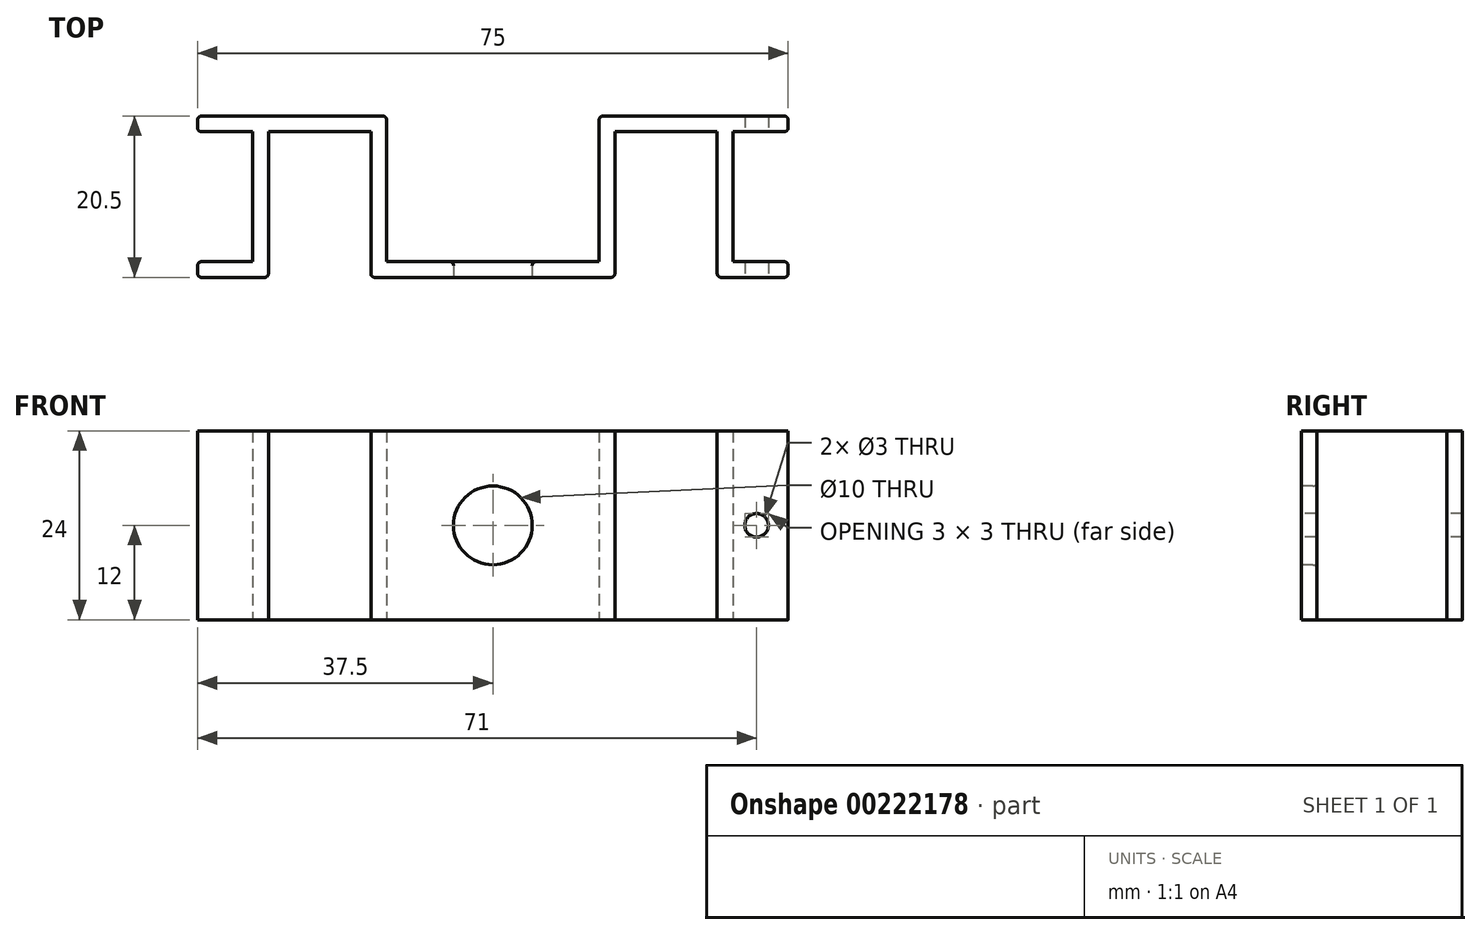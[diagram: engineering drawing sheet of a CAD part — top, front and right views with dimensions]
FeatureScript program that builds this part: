
annotation { "Feature Type Name" : "Feature", "Feature Type Description" : "" }
export const myFeature = defineFeature(function(context is Context, id is Id, definition is map)
    precondition{}
    {
        {
            var Q0;
            Q0=qCreatedBy(makeId("Top.planeOp"),FACE);
            var sketch = newSketch(context, id + "F0", { "sketchPlane" : qUnion([Q0])});
            skLineSegment(sketch, "E0", {"start": v(0, 0) * mm, "end": v(15.5, 0) * mm});
            skLineSegment(sketch, "E1", {"start": v(13.5, 20.5) * mm, "end": v(37.5, 20.5) * mm});
            skLineSegment(sketch, "E2", {"start": v(37.5, 20.5) * mm, "end": v(37.5, 18.5) * mm});
            skLineSegment(sketch, "E3", {"start": v(37.5, 18.5) * mm, "end": v(30.5, 18.5) * mm});
            skLineSegment(sketch, "E4", {"start": v(30.5, 18.5) * mm, "end": v(30.5, 2) * mm});
            skLineSegment(sketch, "E5", {"start": v(30.5, 2) * mm, "end": v(37.5, 2) * mm});
            skLineSegment(sketch, "E6", {"start": v(37.5, 2) * mm, "end": v(37.5, 0) * mm});
            skLineSegment(sketch, "E7", {"start": v(37.5, 0) * mm, "end": v(28.5, 0) * mm});
            skLineSegment(sketch, "E8", {"start": v(28.5, 0) * mm, "end": v(28.5, 18.5) * mm});
            skLineSegment(sketch, "E9", {"start": v(28.5, 18.5) * mm, "end": v(15.5, 18.5) * mm});
            skLineSegment(sketch, "E10", {"start": v(15.5, 18.5) * mm, "end": v(15.5, 0) * mm});
            skLineSegment(sketch, "E11", {"start": v(13.5, 2) * mm, "end": v(0, 2) * mm});
            skLineSegment(sketch, "E12", {"start": v(13.5, 2) * mm, "end": v(13.5, 20.5) * mm});
            skLineSegment(sketch, "E13.MirrorCS", {"start": v(0, 0) * mm, "end": v(-15.5, 0) * mm});
            skLineSegment(sketch, "E14.MirrorCS", {"start": v(-28.5, 18.5) * mm, "end": v(-15.5, 18.5) * mm});
            skLineSegment(sketch, "E15.MirrorCS", {"start": v(-37.5, 18.5) * mm, "end": v(-30.5, 18.5) * mm});
            skLineSegment(sketch, "E16.MirrorCS", {"start": v(-30.5, 2) * mm, "end": v(-37.5, 2) * mm});
            skLineSegment(sketch, "E17.MirrorCS", {"start": v(-15.5, 18.5) * mm, "end": v(-15.5, 0) * mm});
            skLineSegment(sketch, "E18.MirrorCS", {"start": v(-37.5, 2) * mm, "end": v(-37.5, 0) * mm});
            skLineSegment(sketch, "E19.MirrorCS", {"start": v(-37.5, 20.5) * mm, "end": v(-37.5, 18.5) * mm});
            skLineSegment(sketch, "E20.MirrorCS", {"start": v(-13.5, 2) * mm, "end": v(0, 2) * mm});
            skLineSegment(sketch, "E21.MirrorCS", {"start": v(-30.5, 18.5) * mm, "end": v(-30.5, 2) * mm});
            skLineSegment(sketch, "E22.MirrorCS", {"start": v(-28.5, 0) * mm, "end": v(-28.5, 18.5) * mm});
            skLineSegment(sketch, "E23.MirrorCS", {"start": v(-13.5, 2) * mm, "end": v(-13.5, 20.5) * mm});
            skLineSegment(sketch, "E24.MirrorCS", {"start": v(-13.5, 20.5) * mm, "end": v(-37.5, 20.5) * mm});
            skLineSegment(sketch, "E25.MirrorCS", {"start": v(-37.5, 0) * mm, "end": v(-28.5, 0) * mm});
            skPoint(sketch, "E26.orphan", {"position": v(0, 2) * mm});
            skSolve(sketch);
        }
        {
            var Q0;
            Q0=makeQuery(id+"F0.imprint","IMPRINT",FACE,{"disambiguationData":[TD([[makeQuery(id+"F0.imprint","IMPRINT",EDGE,{"derivedFrom":sQuery(id+"F0.wireOp",EDGE,"E0")}),1.0]])]});
            extrude(context, id + "F1", {"entities" : qUnion([Q0]), "depth" : 24 * mm});
        }
        {
            var Q0;
            Q0=makeQuery(id+"F1.opExtrude","SWEPT_FACE",FACE,{"disambiguationData":[OSD([sQuery(id+"F0.wireOp",EDGE,"E7")])]});
            var sketch = newSketch(context, id + "F2", { "sketchPlane" : qUnion([Q0])});
            skCircle(sketch, "E27", {"center": v(33.5, 12) * mm, "radius": 1.5 * mm});
            skCircle(sketch, "E28", {"center": v(0, 12) * mm, "radius": 5 * mm});
            skCircle(sketch, "E29.MirrorC", {"center": v(-33.5, 12) * mm, "radius": 1.5 * mm});
            skLineSegment(sketch, "E30", {"start": v(-41.57, 12) * mm, "end": v(-33.43, 12) * mm, "construction": true});
            skPoint(sketch, "E31", {"position": v(37.5, 12) * mm});
            skSolve(sketch);
        }
        {
            var Q0;
            Q0=makeQuery(id+"F2.imprint","IMPRINT",FACE,{"disambiguationData":[TD([[makeQuery(id+"F2.imprint","IMPRINT",EDGE,{"derivedFrom":sQuery(id+"F2.wireOp",EDGE,"E29.MirrorC")}),-1.0]])]});
            var Q1;
            Q1=makeQuery(id+"F2.imprint","IMPRINT",FACE,{"disambiguationData":[TD([[makeQuery(id+"F2.imprint","IMPRINT",EDGE,{"derivedFrom":sQuery(id+"F2.wireOp",EDGE,"E28")}),1.0]])]});
            var Q2;
            Q2=makeQuery(id+"F2.imprint","IMPRINT",FACE,{"disambiguationData":[TD([[makeQuery(id+"F2.imprint","IMPRINT",EDGE,{"derivedFrom":sQuery(id+"F2.wireOp",EDGE,"E27")}),1.0]])]});
            extrude(context, id + "F3", {"entities" : qUnion([Q0, Q1, Q2]), "operationType" : NewBodyOperationType.REMOVE, "oppositeDirection" : true, "depth" : 25 * mm});
        }
        {
            var Q0;
            Q0=makeQuery(id+"F1.opExtrude","SWEPT_EDGE",EDGE,{"disambiguationData":[OSD([sQuery(id+"F0.wireOp",EDGE,"E23.MirrorCS"),sQuery(id+"F0.wireOp",EDGE,"E24.MirrorCS")])]});
            var Q1;
            Q1=makeQuery(id+"F1.opExtrude","SWEPT_EDGE",EDGE,{"disambiguationData":[OSD([sQuery(id+"F0.wireOp",EDGE,"E1"),sQuery(id+"F0.wireOp",EDGE,"E12")])]});
            var Q2;
            Q2=makeQuery(id+"F1.opExtrude","SWEPT_EDGE",EDGE,{"disambiguationData":[OSD([sQuery(id+"F0.wireOp",EDGE,"E0"),sQuery(id+"F0.wireOp",EDGE,"E10")])]});
            var Q3;
            Q3=makeQuery(id+"F1.opExtrude","SWEPT_EDGE",EDGE,{"disambiguationData":[OSD([sQuery(id+"F0.wireOp",EDGE,"E22.MirrorCS"),sQuery(id+"F0.wireOp",EDGE,"E25.MirrorCS")])]});
            var Q4;
            Q4=makeQuery(id+"F1.opExtrude","SWEPT_EDGE",EDGE,{"disambiguationData":[OSD([sQuery(id+"F0.wireOp",EDGE,"E13.MirrorCS"),sQuery(id+"F0.wireOp",EDGE,"E17.MirrorCS")])]});
            var Q5;
            Q5=makeQuery(id+"F1.opExtrude","SWEPT_EDGE",EDGE,{"disambiguationData":[OSD([sQuery(id+"F0.wireOp",EDGE,"E7"),sQuery(id+"F0.wireOp",EDGE,"E8")])]});
            var Q6;
            Q6=makeQuery(id+"F1.opExtrude","SWEPT_EDGE",EDGE,{"disambiguationData":[OSD([sQuery(id+"F0.wireOp",EDGE,"E1"),sQuery(id+"F0.wireOp",EDGE,"E2")])]});
            var Q7;
            Q7=makeQuery(id+"F1.opExtrude","SWEPT_EDGE",EDGE,{"disambiguationData":[OSD([sQuery(id+"F0.wireOp",EDGE,"E2"),sQuery(id+"F0.wireOp",EDGE,"E3")])]});
            var Q8;
            Q8=makeQuery(id+"F1.opExtrude","SWEPT_EDGE",EDGE,{"disambiguationData":[OSD([sQuery(id+"F0.wireOp",EDGE,"E5"),sQuery(id+"F0.wireOp",EDGE,"E6")])]});
            var Q9;
            Q9=makeQuery(id+"F1.opExtrude","SWEPT_EDGE",EDGE,{"disambiguationData":[OSD([sQuery(id+"F0.wireOp",EDGE,"E6"),sQuery(id+"F0.wireOp",EDGE,"E7")])]});
            var Q10;
            Q10=makeQuery(id+"F1.opExtrude","SWEPT_EDGE",EDGE,{"disambiguationData":[OSD([sQuery(id+"F0.wireOp",EDGE,"E19.MirrorCS"),sQuery(id+"F0.wireOp",EDGE,"E24.MirrorCS")])]});
            var Q11;
            Q11=makeQuery(id+"F1.opExtrude","SWEPT_EDGE",EDGE,{"disambiguationData":[OSD([sQuery(id+"F0.wireOp",EDGE,"E15.MirrorCS"),sQuery(id+"F0.wireOp",EDGE,"E19.MirrorCS")])]});
            var Q12;
            Q12=makeQuery(id+"F1.opExtrude","SWEPT_EDGE",EDGE,{"disambiguationData":[OSD([sQuery(id+"F0.wireOp",EDGE,"E16.MirrorCS"),sQuery(id+"F0.wireOp",EDGE,"E18.MirrorCS")])]});
            var Q13;
            Q13=makeQuery(id+"F1.opExtrude","SWEPT_EDGE",EDGE,{"disambiguationData":[OSD([sQuery(id+"F0.wireOp",EDGE,"E18.MirrorCS"),sQuery(id+"F0.wireOp",EDGE,"E25.MirrorCS")])]});
            var Q14;
            Q14=makeQuery(id+"F3.boolean.opBoolean","COPY",EDGE,{"derivedFrom":makeQuery(id+"F3.opExtrude","CAP_EDGE",EDGE,{"disambiguationData":[OSD([sQuery(id+"F2.wireOp",EDGE,"E28")])],"isStart":true})});
            var Q15;
            Q15=makeQuery(id+"F3.boolean.opBoolean","INTERSECT",EDGE,{"derivedFrom":[makeQuery(id+"F1.opExtrude","SWEPT_FACE",FACE,{"disambiguationData":[OSD([sQuery(id+"F0.wireOp",EDGE,"E11"),sQuery(id+"F0.wireOp",EDGE,"E20.MirrorCS")])]}),makeQuery(id+"F3.opExtrude","SWEPT_FACE",FACE,{"disambiguationData":[OSD([sQuery(id+"F2.wireOp",EDGE,"E28")])]})]});
            fillet(context, id + "F4", {"entities" : qUnion([Q0, Q1, Q2, Q3, Q4, Q5, Q6, Q7, Q8, Q9, Q10, Q11, Q12, Q13, Q14, Q15]), "radius" : .5 * mm, "tangentPropagation" : true, "allowEdgeOverflow" : false});
        }
    });
